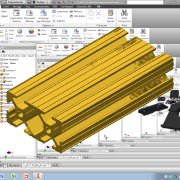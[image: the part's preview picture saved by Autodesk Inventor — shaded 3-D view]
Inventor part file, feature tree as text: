
AUTODESK INVENTOR PART (.ipt)
format: ipt  version: 2015 SP1 (Build 190203100, 203)  size: 478,208 bytes
history: native  units: in
note: dims shown in document units (in); Inventor stores cm internally (conversion verified against a paired STEP export)
features: extrude x1, plane x1, imported_body x1, sketch x1
ambient origin geometry x8: Origin, YZ Plane, XZ Plane, XY Plane, X Axis, Y Axis, Z Axis, Center Point
bodies: Body1 (feature_tree)
feature tree (4):
  extrude  "Extrusion1"  [1 undecoded]
  plane  "Work Plane2"
  imported_body  "Base1"
  sketch  "Sketch1"  dims[d0=3.0in d1=0.0in]
note: 1 required parameter value undecoded (feature->parameter linkage not recoverable at this tier; creation-order binding heuristic only, values carry confidence <= 0.55)
